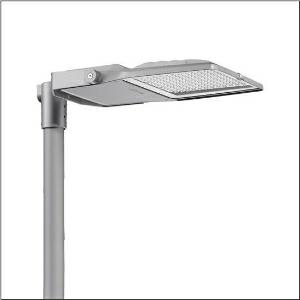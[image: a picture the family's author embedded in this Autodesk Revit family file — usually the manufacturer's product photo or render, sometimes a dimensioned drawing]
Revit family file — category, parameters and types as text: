
# Revit family: floodlight_fl_21_midi___pl64_5xa7781f4e3a_dc39
name_source: partatom
category: Lighting Fixtures
units: mm (PartAtom-declared; Revit-internal decimal feet)

## family parameters
Cut with Voids When Loaded = No
Host = Face
Light Source = No
Part Type = Normal
Room Calculation Point = No
Round Connector Dimension = Use Diameter
Shared = No

## types (1)
- --- (1 x LED, 36050 lm, 270.2 W, 4000K)
    Apparent Load = 270 VA
    CIE Flux Codes = 28 80 98 100 100
    Color Rendering = 70
    Color Temperature = 4000K
    Default Elevation = 1800 mm
    Description = Floodlight FL 21 midi, floodlight, primary light control with lens, of PMMA, primary optical cover: protective disc, of toughened safety glass, transparent, light distribution: PL64, light emission: direct distribution, installation type: surface-mounted, LED, High Power LED, rated luminous flux: 36.050lm, luminous efficacy: 133lm/W, light colour: 740, colour temperature: 4000K, control gear: ECG iQ, control: optimised constant luminous flux control (CLO 2.0), Desk-Remote (wireless, voltage-free reading and setting of iQ features in the workshop via application-optimized NFC function/RFID function), Light-Fading, Smart-Wire, Night-Set, Lumen-Switch, Temp-Guard, Auto-Match, with terminal, 6-pole, mains connection: 220..240V, AC, 50/60Hz, start of lifetime: 270W, end of lifetime: 286W, reduction: 133W, luminaire housing, of diecast aluminium, powder-coated, Siteco® metallic grey (DB 702S), corrosivity category C5 according to DIN EN ISO 12944, mast bracket, of steel, galvanised, powder-coated, Siteco® metallic grey (DB 702S), protection rating (complete): IP66, insulation class (complete): insulation class I (protective earthing), certification: CE, protection symbol: D, impact resistance: IK08, permissible operating ambient temperature: -40..+40°C, permissible operating ambient temperature for outdoor applications: -40..+50°C, standard: DIN EN 12944, packaging unit: 1 piece

Light Distribution: PL64
    Height = 76 mm
    Lamp = 1 x LED
    Lamp Light Flux = 36050 lm
    Lamp Power = 270.2 W
    Lamp count = 1
    Length = 657 mm
    Luminous efficacy = 133 lm/W
    Manufacturer = Siteco
    ModVariant = No
    Model = 5XA7781F4E3A
    Number of Poles = 1
    OnlyDefault = Yes
    Power Factor = 1
    Product Name = Floodlight FL 21 midi | PL64
    Product group = floodlight | pylon top
    ProductGroupID = 6101
    Protection Class = Protection class I
    Protection Degree = IP 66
    RLX_Detail_Level = 1
    RlxData = <blob elided: 153497 chars, md5=114dadfb>
    Socket = socket
    Standby Power = 0 W
    System Light Flux = 36050 lm
    System Power = 270 W
    Type Comments = factory setting: luminous flux: 100 % | dim-lin: 254 | 620 mA
    Type Image = l_1007123.jpg
    URL = http://relux.com
    VarID = @adj_015271
    Voltage = 0 V
    Weight = 0.00 kg
    Width = 442 mm

## geometry (parser evidence)
native form markers: Blend x4, Sweep x13
no freeform markers — native parametric forms only
